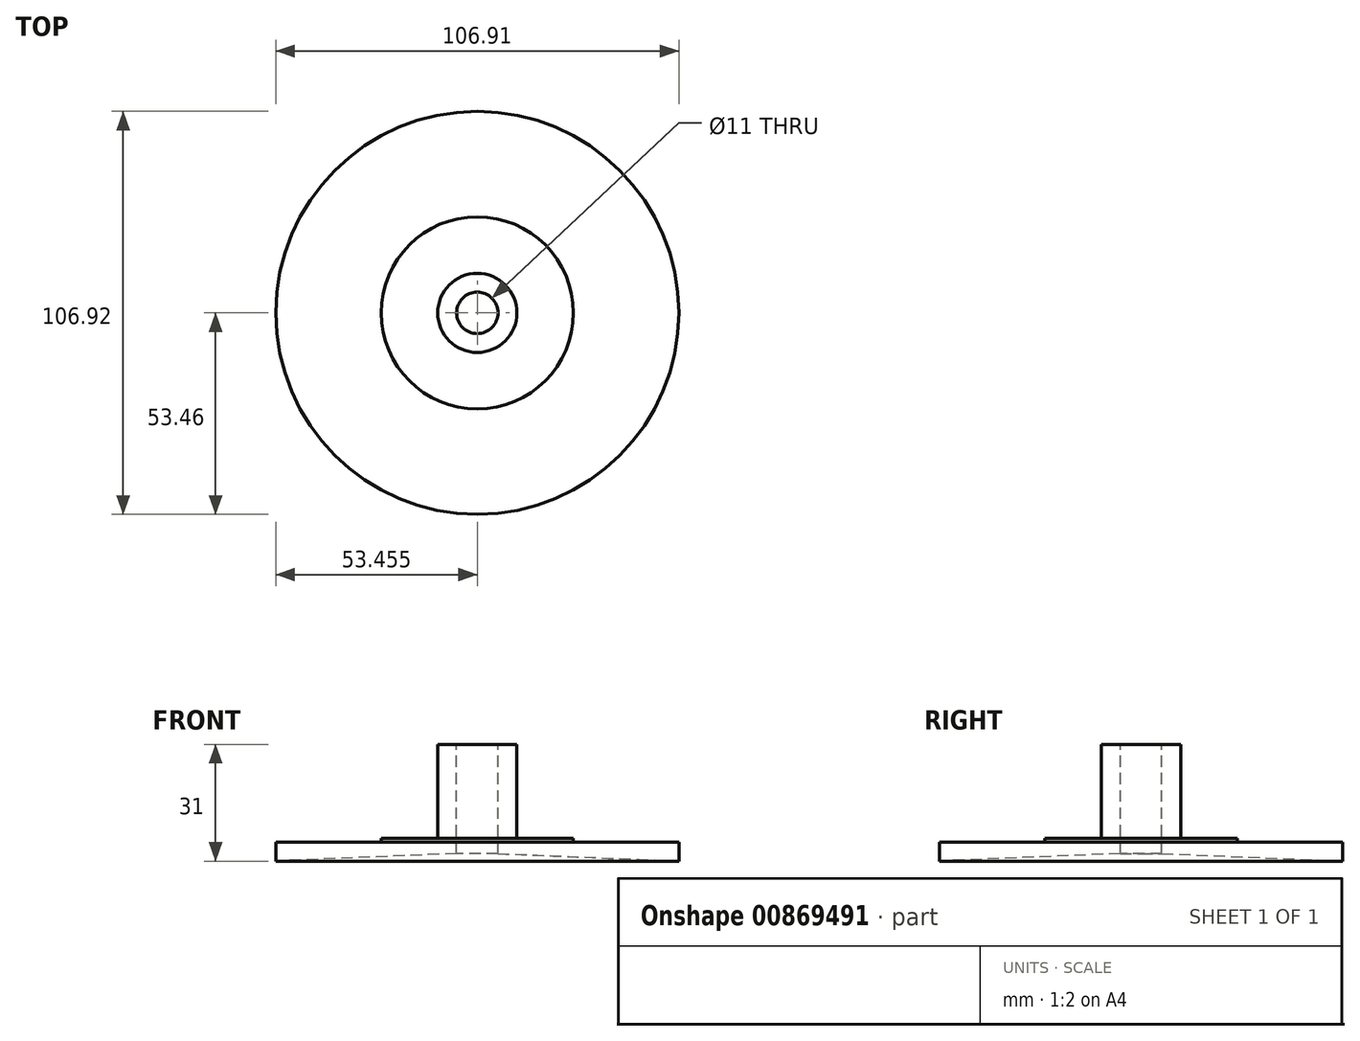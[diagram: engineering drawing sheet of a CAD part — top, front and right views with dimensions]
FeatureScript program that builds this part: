
annotation { "Feature Type Name" : "Feature", "Feature Type Description" : "" }
export const myFeature = defineFeature(function(context is Context, id is Id, definition is map)
    precondition{}
    {
        {
            var Q0;
            Q0=qCreatedBy(makeId("Front.planeOp"),FACE);
            var sketch = newSketch(context, id + "F0", { "sketchPlane" : qUnion([Q0])});
            skLineSegment(sketch, "E0", {"start": v(-60.71, -8.09) * mm, "end": v(-60.71, -3.09) * mm});
            skLineSegment(sketch, "E1", {"start": v(-60.71, -3.09) * mm, "end": v(-32.76, -3.09) * mm});
            skLineSegment(sketch, "E2", {"start": v(-32.76, -3.09) * mm, "end": v(-32.76, -2.09) * mm});
            skLineSegment(sketch, "E3", {"start": v(-32.76, -2.09) * mm, "end": v(-17.76, -2.09) * mm});
            skLineSegment(sketch, "E4", {"start": v(-17.76, -2.09) * mm, "end": v(-17.76, 22.91) * mm});
            skLineSegment(sketch, "E5", {"start": v(-17.76, 22.91) * mm, "end": v(-12.76, 22.91) * mm});
            skLineSegment(sketch, "E6", {"start": v(-12.76, 22.91) * mm, "end": v(-12.76, -6.09) * mm});
            skLineSegment(sketch, "E7", {"start": v(-12.76, -6.09) * mm, "end": v(-60.71, -8.09) * mm});
            skLineSegment(sketch, "E8", {"start": v(-7.26, 39.51) * mm, "end": v(-7.26, -24.16) * mm, "construction": true});
            skSolve(sketch);
        }
        {
            var Q0;
            Q0=makeQuery(id+"F0.imprint","IMPRINT",FACE,{"disambiguationData":[TD([[makeQuery(id+"F0.imprint","IMPRINT",EDGE,{"derivedFrom":sQuery(id+"F0.wireOp",EDGE,"E0")}),-1.0]])]});
            var Q1;
            Q1=sQuery(id+"F0.wireOp",EDGE,"E8");
            revolve(context, id + "F1", {"surfaceOperationType" : NewSurfaceOperationType.NEW, "entities" : qUnion([Q0]), "axis" : qUnion([Q1]), "revolveType" : RevolveType.FULL});
        }
    });
